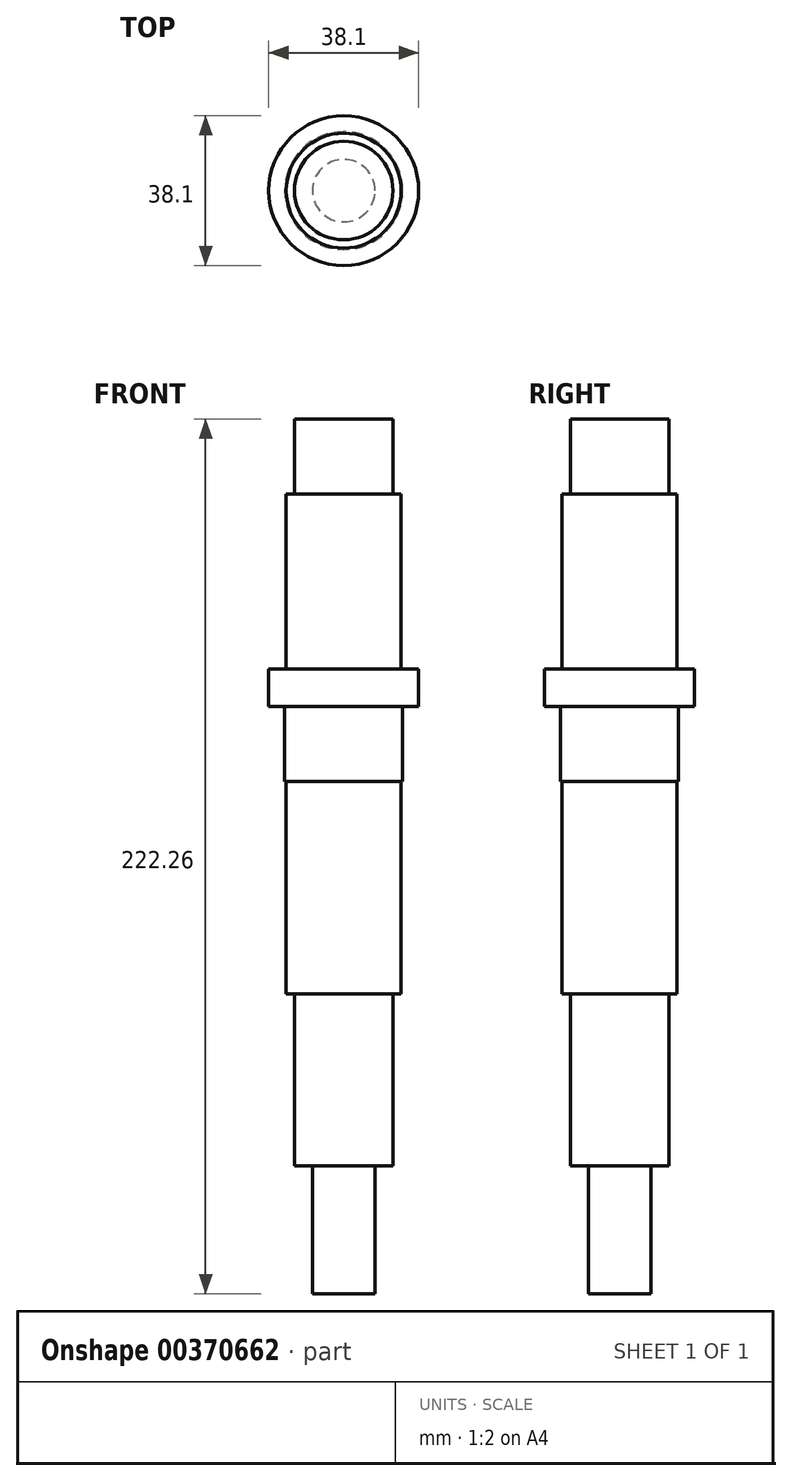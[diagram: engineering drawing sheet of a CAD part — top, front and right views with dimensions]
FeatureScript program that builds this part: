
annotation { "Feature Type Name" : "Feature", "Feature Type Description" : "" }
export const myFeature = defineFeature(function(context is Context, id is Id, definition is map)
    precondition{}
    {
        {
            var Q0;
            Q0=qCreatedBy(makeId("Front.planeOp"),FACE);
            var sketch = newSketch(context, id + "F0", { "sketchPlane" : qUnion([Q0])});
            skLineSegment(sketch, "E0", {"start": v(0, 111.13) * mm, "end": v(0, -111.13) * mm});
            skLineSegment(sketch, "E1", {"start": v(0, -111.13) * mm, "end": v(7.94, -111.13) * mm});
            skLineSegment(sketch, "E2", {"start": v(7.94, -111.13) * mm, "end": v(7.94, -78.58) * mm});
            skLineSegment(sketch, "E3", {"start": v(7.94, -78.58) * mm, "end": v(12.5, -78.58) * mm});
            skLineSegment(sketch, "E4", {"start": v(12.5, -78.58) * mm, "end": v(12.5, -34.92) * mm});
            skLineSegment(sketch, "E5", {"start": v(12.5, -34.92) * mm, "end": v(14.6, -34.92) * mm});
            skLineSegment(sketch, "E6", {"start": v(14.6, -34.92) * mm, "end": v(14.6, 19.05) * mm});
            skLineSegment(sketch, "E7", {"start": v(14.6, 19.05) * mm, "end": v(14.99, 19.05) * mm});
            skLineSegment(sketch, "E8", {"start": v(14.99, 19.05) * mm, "end": v(14.99, 38.1) * mm});
            skLineSegment(sketch, "E9", {"start": v(14.99, 38.1) * mm, "end": v(19.05, 38.1) * mm});
            skLineSegment(sketch, "E10", {"start": v(19.05, 38.1) * mm, "end": v(19.05, 47.62) * mm});
            skLineSegment(sketch, "E11", {"start": v(19.05, 47.62) * mm, "end": v(14.6, 47.62) * mm});
            skLineSegment(sketch, "E12", {"start": v(14.6, 47.62) * mm, "end": v(14.6, 92.08) * mm});
            skLineSegment(sketch, "E13", {"start": v(14.6, 92.08) * mm, "end": v(12.5, 92.08) * mm});
            skLineSegment(sketch, "E14", {"start": v(12.5, 92.08) * mm, "end": v(12.5, 111.13) * mm});
            skLineSegment(sketch, "E15", {"start": v(12.5, 111.13) * mm, "end": v(0, 111.13) * mm});
            skSolve(sketch);
        }
        {
            var Q0;
            Q0=makeQuery(id+"F0.imprint","IMPRINT",FACE,{"disambiguationData":[TD([[makeQuery(id+"F0.imprint","IMPRINT",EDGE,{"derivedFrom":sQuery(id+"F0.wireOp",EDGE,"E0")}),1.0]])]});
            var Q1;
            Q1=sQuery(id+"F0.wireOp",EDGE,"E0");
            revolve(context, id + "F1", {"entities" : qUnion([Q0]), "axis" : qUnion([Q1]), "revolveType" : RevolveType.FULL});
        }
    });
